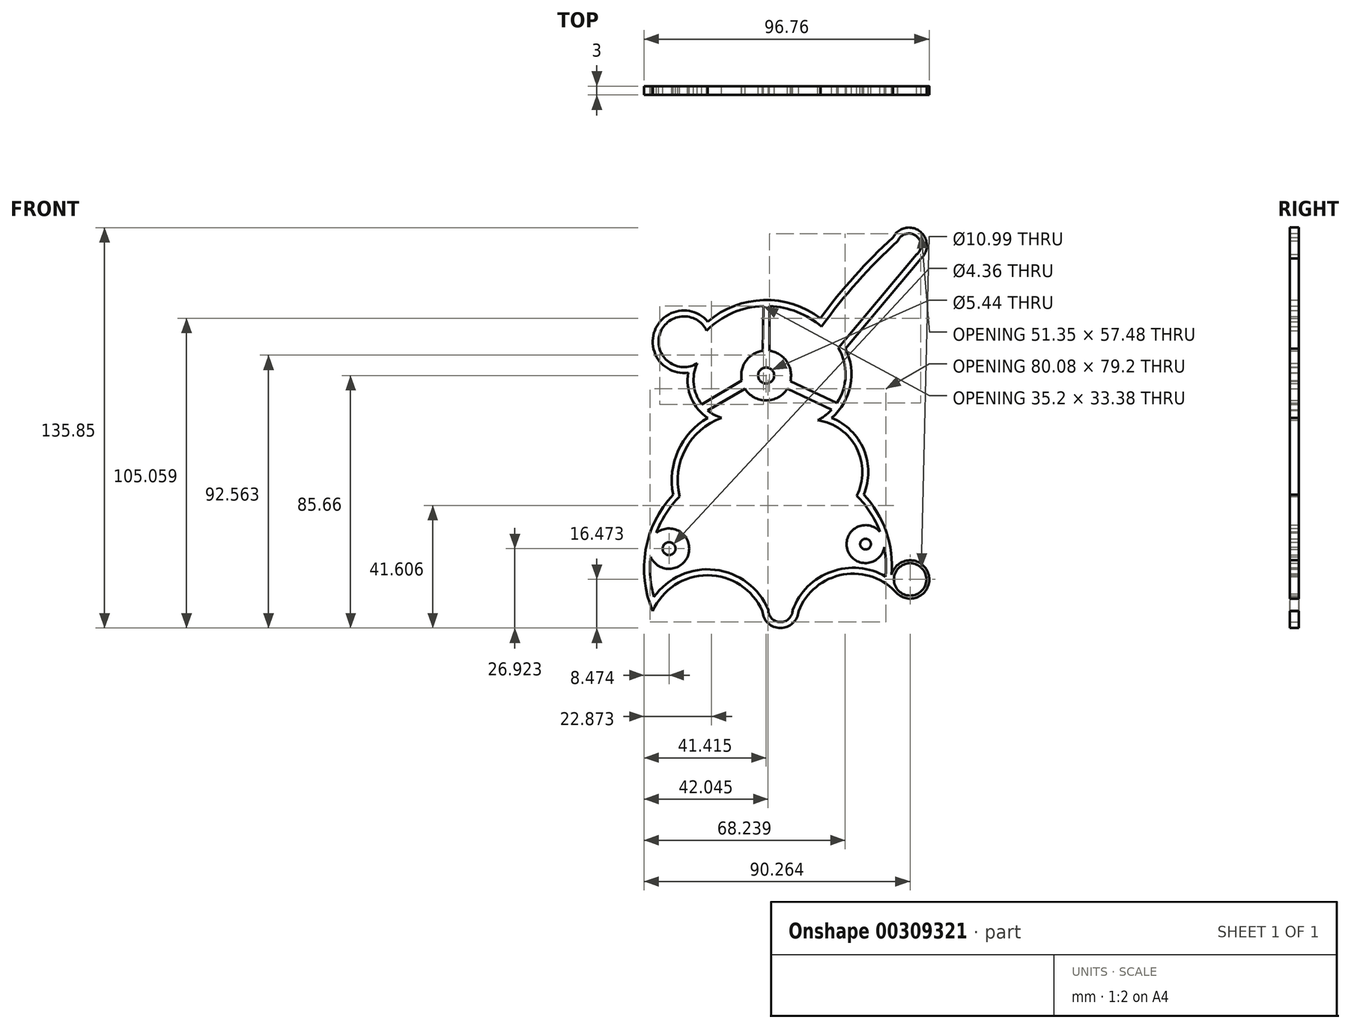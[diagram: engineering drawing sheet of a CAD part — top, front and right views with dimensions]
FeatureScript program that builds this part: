
annotation { "Feature Type Name" : "Feature", "Feature Type Description" : "" }
export const myFeature = defineFeature(function(context is Context, id is Id, definition is map)
    precondition{}
    {
        {
            var Q0;
            Q0=qCreatedBy(makeId("Front.planeOp"),FACE);
            var sketch = newSketch(context, id + "F0", { "sketchPlane" : qUnion([Q0])});
            skArc(sketch, "E0", {"start": v(38.36, -38.04) * mm, "mid": v(48.78, -31.14) * mm, "end": v(36.29, -31.56) * mm});
            skArc(sketch, "E1", {"start": v(36.29, -31.56) * mm, "mid": v(34.48, -16.94) * mm, "end": v(26.87, -4.32) * mm});
            skArc(sketch, "E2", {"start": v(26.87, -4.32) * mm, "mid": v(26.85, 10.97) * mm, "end": v(15.96, 21.7) * mm});
            skArc(sketch, "E3", {"start": v(-26.04, 54.38) * mm, "mid": v(-44.03, 51.33) * mm, "end": v(-32.69, 37.03) * mm});
            skArc(sketch, "E4", {"start": v(-26.04, 21.7) * mm, "mid": v(-36.08, 10.57) * mm, "end": v(-37.79, -4.32) * mm});
            skArc(sketch, "E5", {"start": v(-37.79, -4.32) * mm, "mid": v(-47.12, -23.07) * mm, "end": v(-44.72, -43.87) * mm});
            skArc(sketch, "E6", {"start": v(-7.54, -43.87) * mm, "mid": v(-26.13, -31.68) * mm, "end": v(-44.72, -43.87) * mm});
            skArc(sketch, "E7", {"start": v(-7.54, -43.87) * mm, "mid": v(-1.4, -49.59) * mm, "end": v(4.75, -43.87) * mm});
            skArc(sketch, "E8", {"start": v(38.36, -38.04) * mm, "mid": v(19.9, -31.46) * mm, "end": v(4.75, -43.87) * mm});
            skArc(sketch, "E9", {"start": v(-32.69, 37.03) * mm, "mid": v(-31.64, 28.38) * mm, "end": v(-26.04, 21.7) * mm});
            skArc(sketch, "E10", {"start": v(15.96, 21.7) * mm, "mid": v(22.32, 32.66) * mm, "end": v(20.63, 45.21) * mm});
            skPoint(sketch, "E11.third.point", {"position": v(60.6, 86.21) * mm});
            skPoint(sketch, "E12.start.orphan", {"position": v(12.15, 55.5) * mm});
            skArc(sketch, "E13", {"start": v(12.15, 55.5) * mm, "mid": v(-7.14, 61.67) * mm, "end": v(-26.04, 54.38) * mm});
            skLineSegment(sketch, "E14", {"start": v(20.63, 45.21) * mm, "end": v(46.28, 75.75) * mm});
            skArc(sketch, "E15", {"start": v(36.78, 82.91) * mm, "mid": v(23.8, 69.81) * mm, "end": v(12.15, 55.5) * mm});
            skArc(sketch, "E16", {"start": v(46.28, 75.75) * mm, "mid": v(45.84, 85.04) * mm, "end": v(36.78, 82.91) * mm});
            skPoint(sketch, "E16.third.point", {"position": v(47.61, 82.91) * mm});
            skArc(sketch, "E17.1", {"start": v(-5.56, -43.42) * mm, "mid": v(-1.41, -47.59) * mm, "end": v(2.76, -43.46) * mm});
            skArc(sketch, "E17.2", {"start": v(-5.56, -43.42) * mm, "mid": v(-23.65, -29.82) * mm, "end": v(-44.3, -39.08) * mm});
            skArc(sketch, "E17.3", {"start": v(-35.6, -4.93) * mm, "mid": v(-40.22, -10.72) * mm, "end": v(-43.51, -17.35) * mm});
            skLineSegment(sketch, "E17.4", {"start": v(18.22, 45.45) * mm, "end": v(44.84, 77.15) * mm});
            skArc(sketch, "E17.5", {"start": v(11.3, 20.92) * mm, "mid": v(13.8, 22.5) * mm, "end": v(15.98, 24.5) * mm});
            skArc(sketch, "E17.6", {"start": v(24.48, -4.73) * mm, "mid": v(24.42, 11.45) * mm, "end": v(11.3, 20.92) * mm});
            skArc(sketch, "E17.7", {"start": v(34.3, -31.4) * mm, "mid": v(34.38, -26.76) * mm, "end": v(33.81, -22.16) * mm});
            skArc(sketch, "E17.8", {"start": v(44.84, 77.15) * mm, "mid": v(44.55, 83.51) * mm, "end": v(38.44, 81.71) * mm});
            skArc(sketch, "E17.9", {"start": v(38.44, 81.71) * mm, "mid": v(24.71, 67.84) * mm, "end": v(12.52, 52.6) * mm});
            skArc(sketch, "E17.10", {"start": v(12.52, 52.6) * mm, "mid": v(4.31, 57.65) * mm, "end": v(-5.1, 59.66) * mm});
            skArc(sketch, "E17.11", {"start": v(-26.4, 51.32) * mm, "mid": v(-42.4, 49.9) * mm, "end": v(-29.59, 40.23) * mm});
            skArc(sketch, "E17.12", {"start": v(-29.59, 40.23) * mm, "mid": v(-30.83, 33.05) * mm, "end": v(-28.1, 26.28) * mm});
            skArc(sketch, "E17.13", {"start": v(-21.32, 21.7) * mm, "mid": v(-33.58, 11.12) * mm, "end": v(-35.6, -4.93) * mm});
            skArc(sketch, "E18", {"start": v(34.3, -31.4) * mm, "mid": v(34.28, -31.75) * mm, "end": v(34.3, -32.12) * mm});
            skArc(sketch, "E19.trimOffspring", {"start": v(34.3, -32.12) * mm, "mid": v(15.9, -30.46) * mm, "end": v(2.76, -43.46) * mm});
            skCircle(sketch, "E20", {"center": v(42.6, -33.12) * mm, "radius": 5.5 * mm});
            skArc(sketch, "E21", {"start": v(-45.44, -25.47) * mm, "mid": v(-32.54, -24.25) * mm, "end": v(-43.51, -17.35) * mm});
            skCircle(sketch, "E22", {"center": v(-39.2, -22.67) * mm, "radius": 2.18 * mm});
            skArc(sketch, "E23.trimOffspring", {"start": v(-45.44, -25.47) * mm, "mid": v(-45.55, -32.33) * mm, "end": v(-44.3, -39.08) * mm});
            skArc(sketch, "E24", {"start": v(32.37, -16.97) * mm, "mid": v(21.26, -22.86) * mm, "end": v(33.81, -22.16) * mm});
            skCircle(sketch, "E25", {"center": v(27.46, -21.13) * mm, "radius": 1.81 * mm});
            skArc(sketch, "E26", {"start": v(-7.4, 44.45) * mm, "mid": v(-13.17, 40.94) * mm, "end": v(-14.53, 34.33) * mm});
            skPoint(sketch, "E27.startSnap0", {"position": v(-7.2, 59.66) * mm});
            skLineSegment(sketch, "E28", {"start": v(-28.1, 26.28) * mm, "end": v(-14.53, 34.33) * mm});
            skLineSegment(sketch, "E29", {"start": v(-26.08, 24.21) * mm, "end": v(-13.44, 31.62) * mm});
            skLineSegment(sketch, "E30", {"start": v(0.93, 31.62) * mm, "end": v(15.98, 24.5) * mm});
            skLineSegment(sketch, "E31", {"start": v(1.99, 34.19) * mm, "end": v(17.75, 26.73) * mm});
            skPoint(sketch, "E27.start.orphan", {"position": v(-5.31, 59.66) * mm});
            skPoint(sketch, "E32.start.orphan", {"position": v(-5.31, 44.47) * mm});
            skLineSegment(sketch, "E33", {"start": v(-7.4, 44.45) * mm, "end": v(-7.2, 59.66) * mm});
            skLineSegment(sketch, "E34", {"start": v(-5.1, 44.45) * mm, "end": v(-5.1, 59.66) * mm});
            skArc(sketch, "E35.trimOffspring", {"start": v(-7.2, 59.66) * mm, "mid": v(-17.6, 57.32) * mm, "end": v(-26.4, 51.32) * mm});
            skCircle(sketch, "E36", {"center": v(-6.26, 36.07) * mm, "radius": 2.72 * mm});
            skArc(sketch, "E37.trimOffspring", {"start": v(-13.44, 31.62) * mm, "mid": v(-6.26, 27.62) * mm, "end": v(0.93, 31.62) * mm});
            skArc(sketch, "E38.trimOffspring", {"start": v(1.99, 34.19) * mm, "mid": v(0.64, 40.96) * mm, "end": v(-5.31, 44.47) * mm});
            skArc(sketch, "E39.trimOffspring", {"start": v(17.75, 26.73) * mm, "mid": v(20.7, 36.02) * mm, "end": v(18.22, 45.45) * mm});
            skArc(sketch, "E40.trimOffspring", {"start": v(-26.08, 24.21) * mm, "mid": v(-23.83, 22.71) * mm, "end": v(-21.32, 21.7) * mm});
            skArc(sketch, "E41.trimOffspring", {"start": v(32.37, -16.97) * mm, "mid": v(29.1, -10.41) * mm, "end": v(24.48, -4.73) * mm});
            skSolve(sketch);
        }
        {
            var Q0;
            Q0 = qSketchRegion(id + "F0", true);
            extrude(context, id + "F1", {"entities" : qUnion([Q0]), "depth" : 3 * mm});
        }
    });
